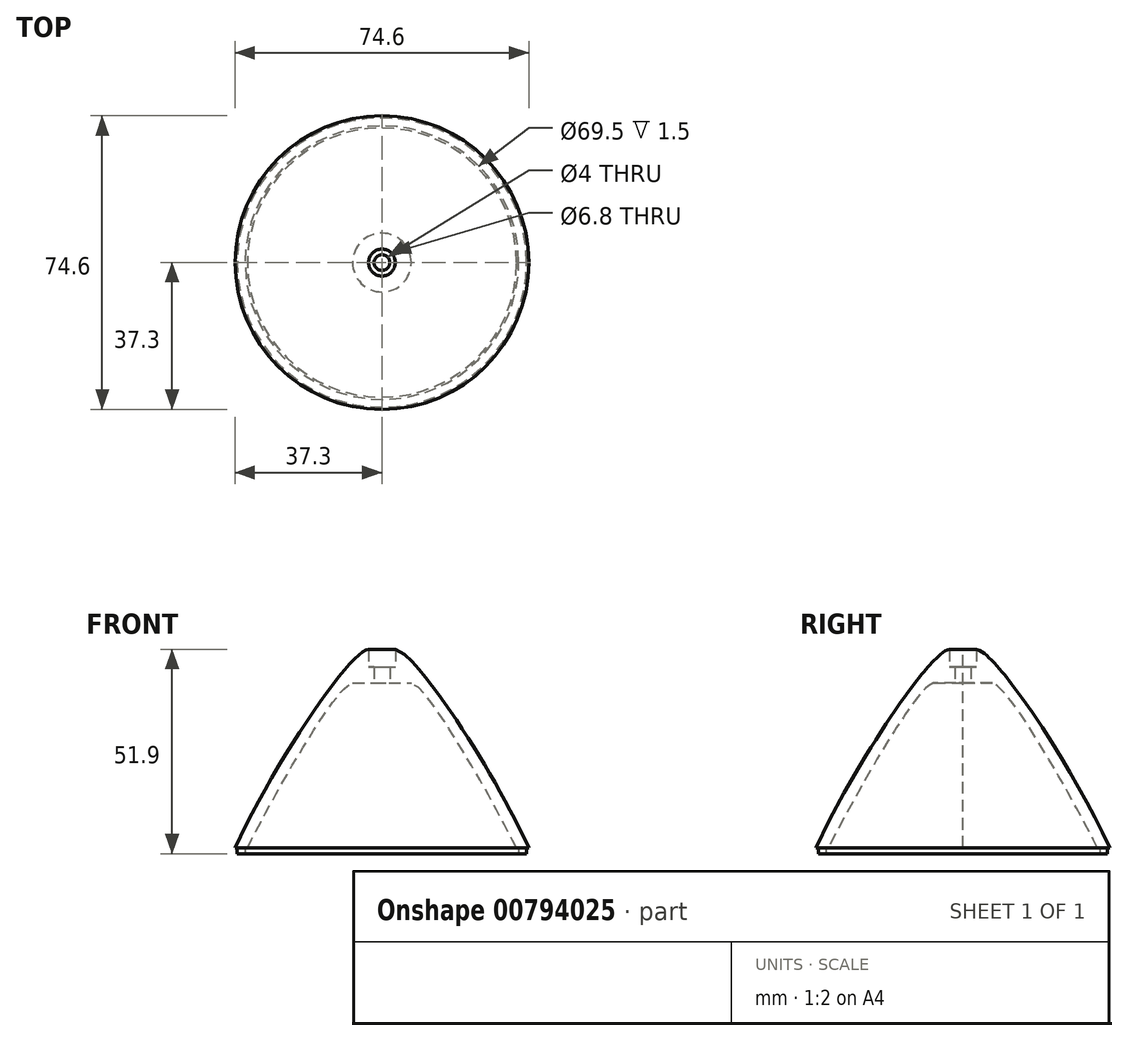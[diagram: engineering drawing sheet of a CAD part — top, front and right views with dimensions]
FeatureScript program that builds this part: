
annotation { "Feature Type Name" : "Feature", "Feature Type Description" : "" }
export const myFeature = defineFeature(function(context is Context, id is Id, definition is map)
    precondition{}
    {
        {
            var Q0;
            Q0=qCreatedBy(makeId("Front.planeOp"),FACE);
            var sketch = newSketch(context, id + "F0", { "sketchPlane" : qUnion([Q0])});
            skLineSegment(sketch, "E0", {"start": v(-37.38, 51.9) * mm, "end": v(-37.38, -5.49) * mm, "construction": true});
            skLineSegment(sketch, "E1", {"start": v(-37.38, 51.9) * mm, "end": v(17.46, 51.9) * mm, "construction": true});
            skLineSegment(sketch, "E2", {"start": v(0, 51.9) * mm, "end": v(-3.4, 51.9) * mm});
            skLineSegment(sketch, "E3", {"start": v(-3.4, 51.9) * mm, "end": v(-3.4, 47.4) * mm});
            skLineSegment(sketch, "E4", {"start": v(-2, 47.44) * mm, "end": v(-2, 43.34) * mm});
            skLineSegment(sketch, "E5", {"start": v(-3.4, 47.4) * mm, "end": v(-2, 47.44) * mm});
            skLineSegment(sketch, "E6", {"start": v(-2, 43.34) * mm, "end": v(-7.46, 43.34) * mm});
            skLineSegment(sketch, "E7", {"start": v(-37.3, 1.5) * mm, "end": v(-34.2, 1.5) * mm});
            skLineSegment(sketch, "E8", {"start": v(-36.75, 1.5) * mm, "end": v(-36.75, 0) * mm});
            skLineSegment(sketch, "E9", {"start": v(-36.75, 0) * mm, "end": v(-34.75, 0) * mm});
            skLineSegment(sketch, "E10", {"start": v(-34.75, 0) * mm, "end": v(-34.75, 1.5) * mm});
            skFitSpline(sketch, "E11", {"points": [v(-37.3, 1.5) * mm, v(-3.4, 51.9) * mm], "startDerivative": vector(29.84, 65.12) * mm, "endDerivative": vector(13.44, 0) * mm});
            skPoint(sketch, "E12", {"position": v(-37.38, 23.2) * mm});
            skFitSpline(sketch, "E13", {"points": [v(-34.2, 1.5) * mm, v(-7.46, 43.34) * mm], "startDerivative": vector(24.1, 47.28) * mm, "endDerivative": vector(12.38, 1.78) * mm});
            skPoint(sketch, "E14", {"position": v(-9.96, 51.9) * mm});
            skSolve(sketch);
        }
        {
            var Q0;
            Q0=qCreatedBy(makeId("Top.planeOp"),FACE);
            var sketch = newSketch(context, id + "F1", { "sketchPlane" : qUnion([Q0])});
            skCircle(sketch, "E15", {"center": v(0, 0) * mm, "radius": 37.05 * mm});
            skSolve(sketch);
        }
        {
            var Q0;
            Q0=makeQuery(id+"F0.imprint","IMPRINT",FACE,{"disambiguationData":[TD([[makeQuery(id+"F0.imprint","IMPRINT",EDGE,{"derivedFrom":sQuery(id+"F0.wireOp",EDGE,"E3")}),-1.0]])]});
            var Q1;
            {var subQ0=sQuery(id+"F0.wireOp",EDGE,"E8");Q1=makeQuery(id+"F0.imprint","IMPRINT",FACE,{"disambiguationData":[TD([[makeQuery(id+"F0.imprint","IMPRINT",EDGE,{"derivedFrom":subQ0}),1.0]])]});}
            var Q2;
            Q2=sQuery(id+"F1.wireOp",EDGE,"E15");
            revolve(context, id + "F2", {"surfaceOperationType" : NewSurfaceOperationType.NEW, "entities" : qUnion([Q0, Q1]), "axis" : qUnion([Q2]), "revolveType" : RevolveType.FULL});
        }
    });
